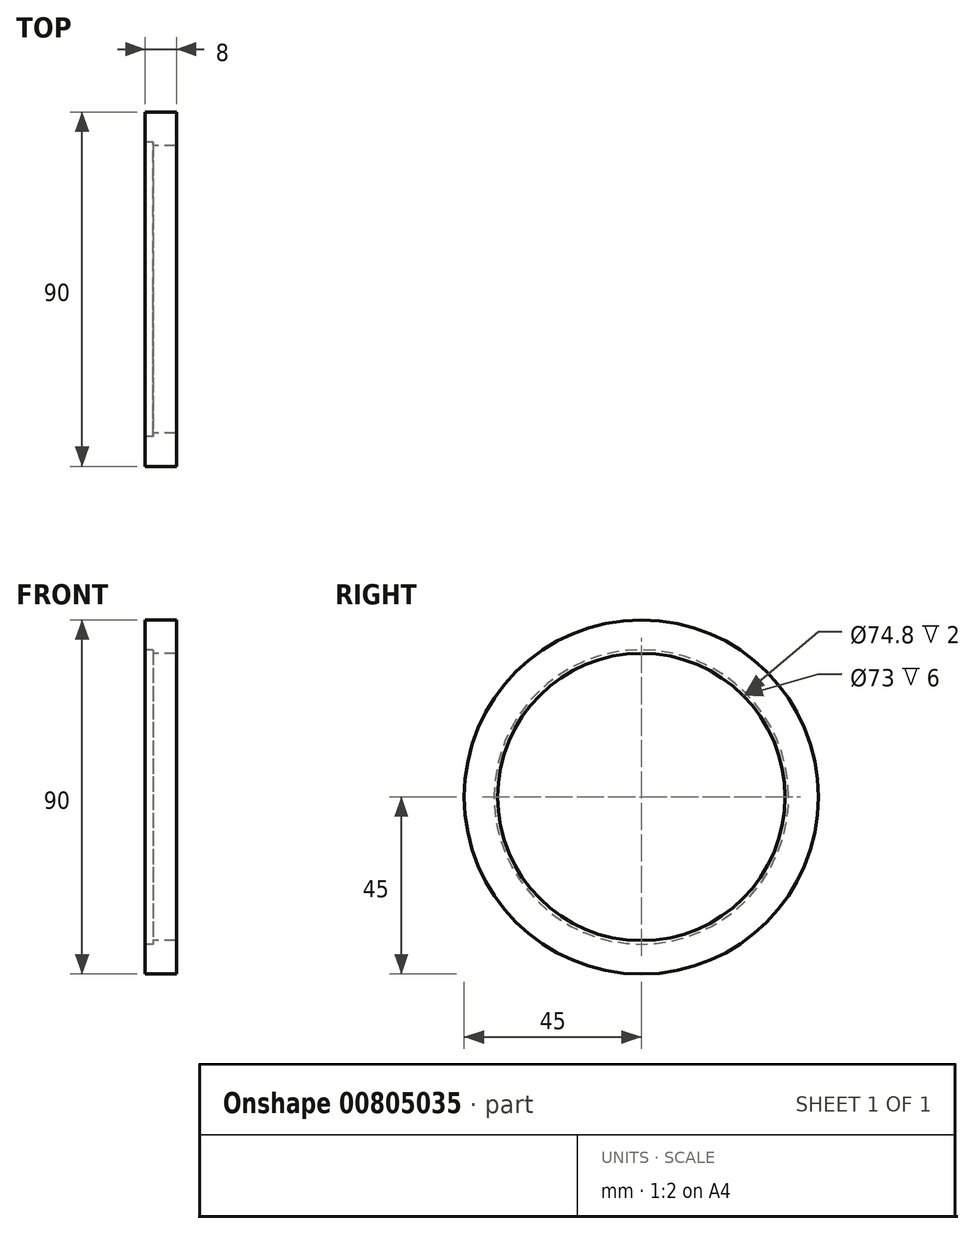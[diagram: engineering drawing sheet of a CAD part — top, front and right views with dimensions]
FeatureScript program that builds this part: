
annotation { "Feature Type Name" : "Feature", "Feature Type Description" : "" }
export const myFeature = defineFeature(function(context is Context, id is Id, definition is map)
    precondition{}
    {
        {
            var Q0;
            Q0=qCreatedBy(makeId("Front.planeOp"),FACE);
            var sketch = newSketch(context, id + "F0", { "sketchPlane" : qUnion([Q0])});
            skLineSegment(sketch, "E0", {"start": v(0, 37.4) * mm, "end": v(0, 45) * mm});
            skLineSegment(sketch, "E1", {"start": v(0, 45) * mm, "end": v(8, 45) * mm});
            skLineSegment(sketch, "E2", {"start": v(8, 45) * mm, "end": v(8, 36.5) * mm});
            skLineSegment(sketch, "E3", {"start": v(8, 36.5) * mm, "end": v(2, 36.5) * mm});
            skLineSegment(sketch, "E4", {"start": v(2, 37.4) * mm, "end": v(2, 36.5) * mm});
            skLineSegment(sketch, "E5", {"start": v(2, 37.4) * mm, "end": v(0, 37.4) * mm});
            skLineSegment(sketch, "E6", {"start": v(0, 0) * mm, "end": v(8, 0) * mm, "construction": true});
            skSolve(sketch);
        }
        {
            var Q0;
            Q0=makeQuery(id+"F0.imprint","IMPRINT",FACE,{"disambiguationData":[TD([[makeQuery(id+"F0.imprint","IMPRINT",EDGE,{"derivedFrom":sQuery(id+"F0.wireOp",EDGE,"E0")}),-1.0]])]});
            var Q1;
            Q1=sQuery(id+"F0.wireOp",EDGE,"E6");
            revolve(context, id + "F1", {"surfaceOperationType" : NewSurfaceOperationType.NEW, "entities" : qUnion([Q0]), "axis" : qUnion([Q1]), "revolveType" : RevolveType.FULL});
        }
    });
